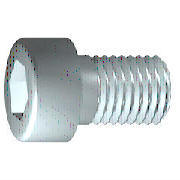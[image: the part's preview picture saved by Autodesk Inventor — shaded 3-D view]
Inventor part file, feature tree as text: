
AUTODESK INVENTOR PART (.ipt)
format: ipt  version: 2017 SP1 (Build 210196100, 196)  size: 184,832 bytes
history: native  units: mm (DEFAULTED — no unit token found)
features: sketch x2, extrude x1, plane x1, fillet x1
ambient origin geometry x7: Origin, YZ Plane, XY Plane, X Axis, Y Axis, Z Axis, Center Point
bodies: Solid1 (feature_tree), Body (feature_tree)
feature tree (5):
  extrude  "Slot"  Depth=3.0mm
  plane  "Work Plane1"
  fillet  "Fillet2"  Radius=3.0mm
  sketch  "Sketch1"  dims[d1=18.0mm d2=0.306825mm d3=3.0mm]
  sketch  "Sketch2"  dims[d4=1.3mm d5=60.0deg d6=3.0mm d7=3.0mm d8=2.886751mm d9=5.5mm d10=90.0deg d11=10.0mm d12=0.0mm d13=18.0mm d14=0.0mm d15=0.306725mm d16=0.306725mm d17=0.3mm d19=0.0mm d26=25.0mm d27=45.0deg d28=0.0mm d29=0.0mm d30=0.1mm]
